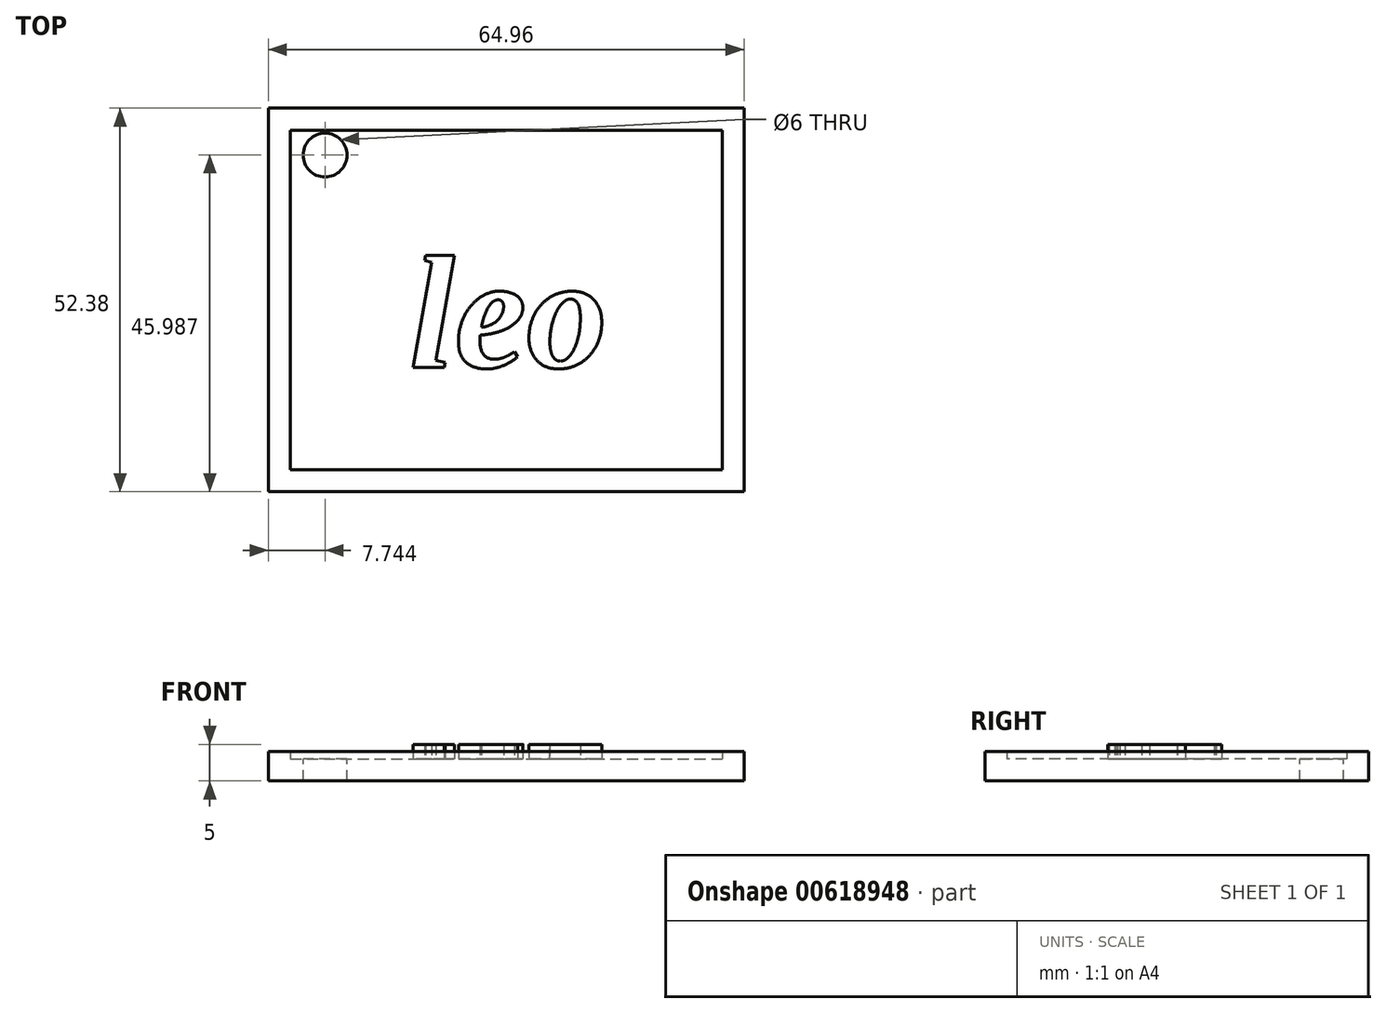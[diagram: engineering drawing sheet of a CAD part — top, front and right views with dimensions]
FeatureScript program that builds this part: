
annotation { "Feature Type Name" : "Feature", "Feature Type Description" : "" }
export const myFeature = defineFeature(function(context is Context, id is Id, definition is map)
    precondition{}
    {
        {
            var Q0;
            Q0=qCreatedBy(makeId("Top.planeOp"),FACE);
            var sketch = newSketch(context, id + "F0", { "sketchPlane" : qUnion([Q0])});
            skLineSegment(sketch, "E0.bottom", {"start": v(0, 0) * mm, "end": v(64.96, 0) * mm});
            skLineSegment(sketch, "E0.top", {"start": v(0, -52.38) * mm, "end": v(64.96, -52.38) * mm});
            skLineSegment(sketch, "E0.left", {"start": v(0, 0) * mm, "end": v(0, -52.38) * mm});
            skLineSegment(sketch, "E0.right", {"start": v(64.96, 0) * mm, "end": v(64.96, -52.38) * mm});
            skSolve(sketch);
        }
        {
            var Q0;
            Q0=makeQuery(id+"F0.imprint","IMPRINT",FACE,{"disambiguationData":[TD([[makeQuery(id+"F0.imprint","IMPRINT",EDGE,{"derivedFrom":sQuery(id+"F0.wireOp",EDGE,"E0.bottom")}),-1.0]])]});
            extrude(context, id + "F1", {"entities" : qUnion([Q0]), "depth" : 4 * mm, "offsetDistance" : 25.4 * mm});
        }
        {
            var Q0;
            Q0=makeQuery(id+"F1.opExtrude","CAP_FACE",FACE,{"disambiguationData":[OSD([sQuery(id+"F0.wireOp",EDGE,"E0.bottom"),sQuery(id+"F0.wireOp",EDGE,"E0.top"),sQuery(id+"F0.wireOp",EDGE,"E0.left"),sQuery(id+"F0.wireOp",EDGE,"E0.right")])],"isStart":false});
            shell(context, id + "F2", {"entities" : qUnion([Q0]), "thickness" : 3 * mm});
        }
        {
            var Q0;
            Q0=makeQuery(id+"F2.opShell","OFFSET_FACE",FACE,{"disambiguationData":[OSD([sQuery(id+"F0.wireOp",EDGE,"E0.bottom"),sQuery(id+"F0.wireOp",EDGE,"E0.top"),sQuery(id+"F0.wireOp",EDGE,"E0.left"),sQuery(id+"F0.wireOp",EDGE,"E0.right")])]});
            var sketch = newSketch(context, id + "F3", { "sketchPlane" : qUnion([Q0])});
            skText(sketch, "E1", { "text": "leo", "fontName": "Tinos-BoldItalic.ttf"});
            const initialGuessF3  = {"E1": [0.0193, -0.0354, 1, 0, 0.0159]};
            skSetInitialGuess(sketch, initialGuessF3);
            skSolve(sketch);
        }
        {
            var Q0;
            Q0 = qSketchRegion(id + "F3", true);
            extrude(context, id + "F4", {"entities" : qUnion([Q0]), "operationType" : NewBodyOperationType.ADD, "depth" : 2 * mm, "offsetDistance" : 25 * mm});
        }
        {
            var Q0;
            {var subQ0=sQuery(id+"F0.wireOp",EDGE,"E0.left");var subQ1=sQuery(id+"F0.wireOp",EDGE,"E0.top");var subQ2=sQuery(id+"F0.wireOp",EDGE,"E0.bottom");var subQ3=sQuery(id+"F0.wireOp",EDGE,"E0.right");Q0=makeQuery(id+"F4.boolean.opBoolean","SPLIT",FACE,{"disambiguationData":[TD([makeQuery(id+"F2.opShell","OFFSET_FACE",FACE,{"disambiguationData":[OSD([subQ2])]})])],"derivedFrom":makeQuery(id+"F2.opShell","OFFSET_FACE",FACE,{"disambiguationData":[OSD([subQ2,subQ1,subQ0,subQ3])]})});}
            var sketch = newSketch(context, id + "F5", { "sketchPlane" : qUnion([Q0])});
            skCircle(sketch, "E2", {"center": v(7.74, -6.4) * mm, "radius": 3.07 * mm});
            skSolve(sketch);
        }
        {
            var Q0;
            Q0=sQuery(id+"F5.wireOp",VERTEX,"E2.center");
            var Q1;
            Q1=makeQuery(id+"F1.opExtrude","SWEPT_BODY",BODY,{"disambiguationData":[OSD([sQuery(id+"F0.wireOp",EDGE,"E0.bottom"),sQuery(id+"F0.wireOp",EDGE,"E0.top"),sQuery(id+"F0.wireOp",EDGE,"E0.left"),sQuery(id+"F0.wireOp",EDGE,"E0.right")])]});
            hole(context, id + "F6", {"style" : HoleStyle.SIMPLE, "endStyle" : HoleEndStyle.THROUGH, "holeDiameter" : 6 * mm, "majorDiameter" : 5 * mm, "isTappedThrough" : true, "tappedDepth" : 12 * mm, "tapClearance" : 3, "locations" : qUnion([Q0]), "scope" : qUnion([Q1])});
        }
    });
